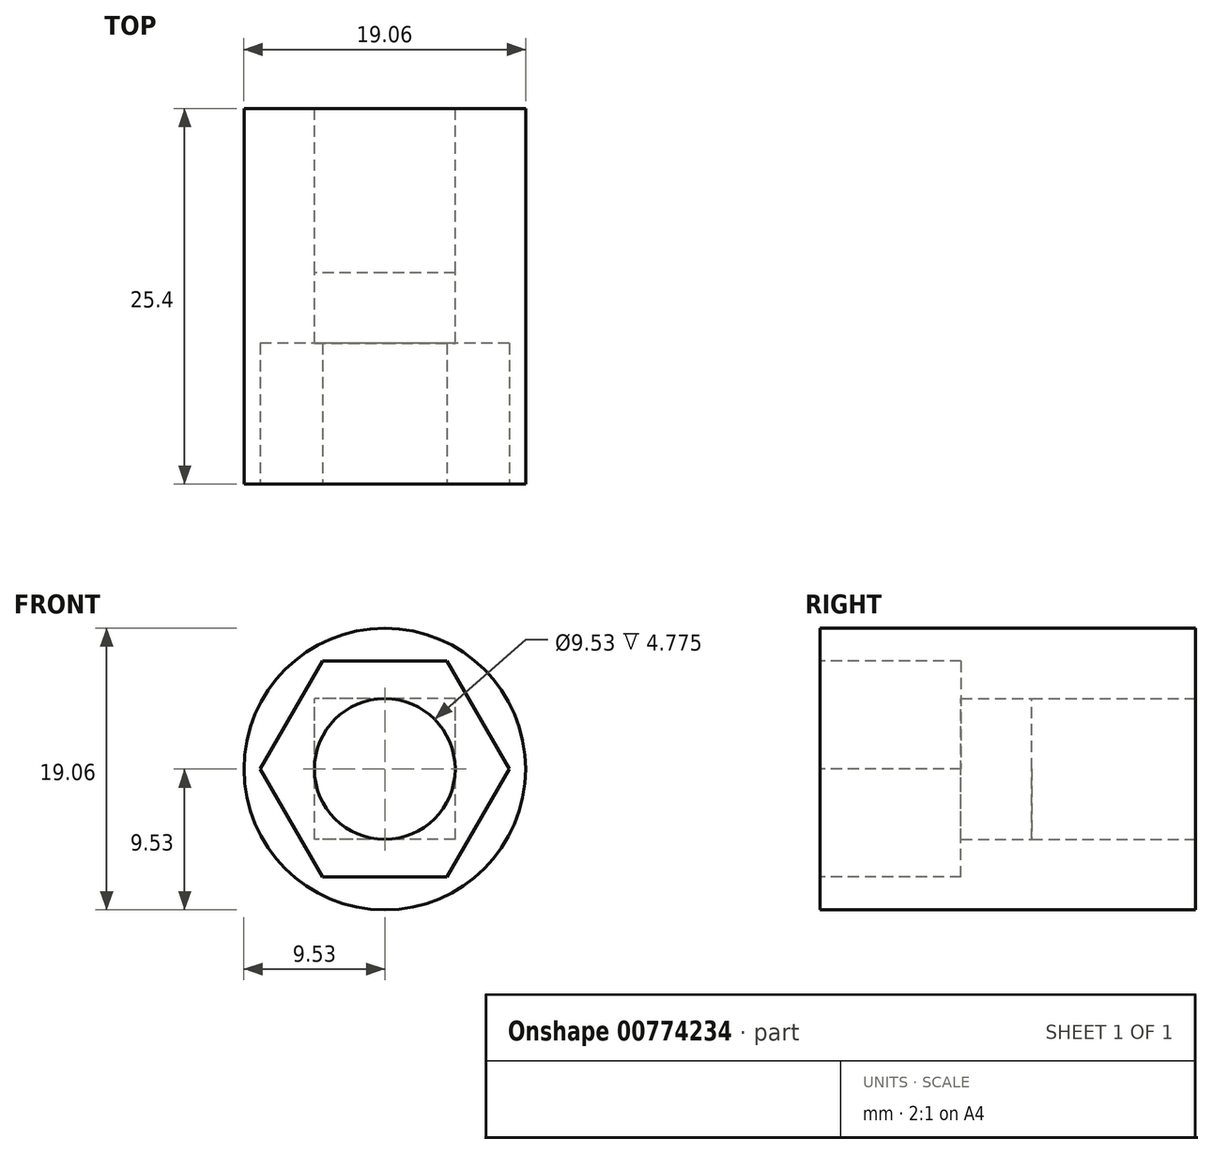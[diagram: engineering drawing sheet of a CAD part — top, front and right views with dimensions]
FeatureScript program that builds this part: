
annotation { "Feature Type Name" : "Feature", "Feature Type Description" : "" }
export const myFeature = defineFeature(function(context is Context, id is Id, definition is map)
    precondition{}
    {
        {
            var Q0;
            Q0=qCreatedBy(makeId("Front.planeOp"),FACE);
            var sketch = newSketch(context, id + "F0", { "sketchPlane" : qUnion([Q0])});
            skCircle(sketch, "E0", {"center": v(0, 0) * mm, "radius": 9.53 * mm});
            skSolve(sketch);
        }
        {
            var Q0;
            Q0=qSketchRegion(id+"F0",true);
            extrude(context, id + "F1", {"entities" : qUnion([Q0]), "depth" : 25.4 * mm});
        }
        {
            var Q0;
            Q0=qCreatedBy(makeId("Front.planeOp"),FACE);
            var sketch = newSketch(context, id + "F2", { "sketchPlane" : qUnion([Q0])});
            skLineSegment(sketch, "E1.bottom", {"start": v(4.76, -4.76) * mm, "end": v(-4.76, -4.76) * mm});
            skLineSegment(sketch, "E1.top", {"start": v(4.76, 4.76) * mm, "end": v(-4.76, 4.76) * mm});
            skLineSegment(sketch, "E1.left", {"start": v(4.76, -4.76) * mm, "end": v(4.76, 4.76) * mm});
            skLineSegment(sketch, "E1.right", {"start": v(-4.76, -4.76) * mm, "end": v(-4.76, 4.76) * mm});
            skPoint(sketch, "E1.middle", {"position": v(0, 0) * mm});
            skCircle(sketch, "E2", {"center": v(0, 0) * mm, "radius": 4.76 * mm});
            skSolve(sketch);
        }
        {
            var Q0;
            {var subQ0=sQuery(id+"F2.wireOp",EDGE,"E2");var subQ1=makeQuery(id+"F2.imprint","INTERSECT",VERTEX,{"derivedFrom":[sQuery(id+"F2.wireOp",EDGE,"E1.top"),subQ0]});Q0=makeQuery(id+"F2.imprint","IMPRINT",FACE,{"disambiguationData":[TD([[makeQuery(id+"F2.imprint","IMPRINT",EDGE,{"disambiguationData":[TD([[subQ1,1.0]])],"derivedFrom":subQ0}),1.0]])]});}
            extrude(context, id + "F3", {"entities" : qUnion([Q0]), "operationType" : NewBodyOperationType.REMOVE, "endBound" : BoundingType.THROUGH_ALL, "depth" : 25.4 * mm});
        }
        {
            var Q0;
            Q0=qSketchRegion(id+"F2",true);
            extrude(context, id + "F4", {"entities" : qUnion([Q0]), "operationType" : NewBodyOperationType.REMOVE, "depth" : 11.1 * mm});
        }
        {
            var Q0;
            Q0=makeQuery(id+"F1.opExtrude","CAP_FACE",FACE,{"disambiguationData":[OSD([sQuery(id+"F0.wireOp",EDGE,"E0")])],"isStart":false});
            var sketch = newSketch(context, id + "F5", { "sketchPlane" : qUnion([Q0])});
            skCircle(sketch, "E3.cCircle", {"center": v(0, 0) * mm, "radius": 7.3 * mm, "construction": true});
            skLineSegment(sketch, "E3.0", {"start": v(-4.22, -7.3) * mm, "end": v(-8.43, 0) * mm});
            skLineSegment(sketch, "E3.1", {"start": v(-8.43, 0) * mm, "end": v(-4.22, 7.3) * mm});
            skLineSegment(sketch, "E3.2", {"start": v(-4.22, 7.3) * mm, "end": v(4.22, 7.3) * mm});
            skLineSegment(sketch, "E3.3", {"start": v(4.22, 7.3) * mm, "end": v(8.43, 0) * mm});
            skLineSegment(sketch, "E3.4", {"start": v(8.43, 0) * mm, "end": v(4.22, -7.3) * mm});
            skLineSegment(sketch, "E3.5", {"start": v(4.22, -7.3) * mm, "end": v(-4.22, -7.3) * mm});
            skPoint(sketch, "E3.0.midPoint", {"position": v(-6.32, -3.65) * mm});
            skSolve(sketch);
        }
        {
            var Q0;
            Q0=qSketchRegion(id+"F5",true);
            extrude(context, id + "F6", {"entities" : qUnion([Q0]), "operationType" : NewBodyOperationType.REMOVE, "oppositeDirection" : true, "depth" : 9.52 * mm});
        }
    });
